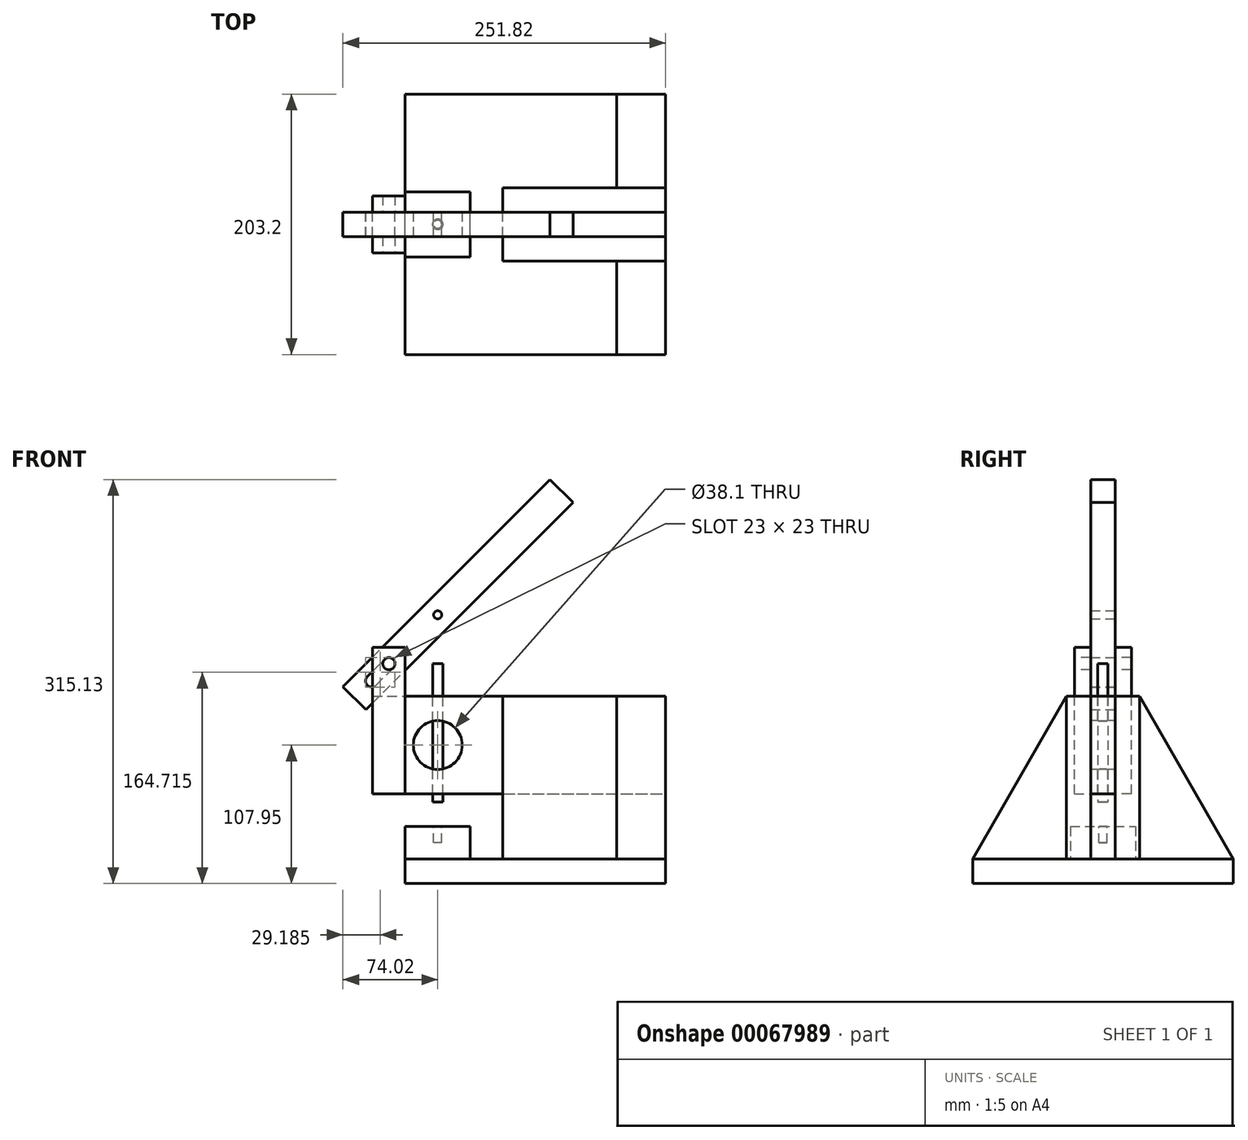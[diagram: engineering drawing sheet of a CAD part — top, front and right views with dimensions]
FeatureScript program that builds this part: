
annotation { "Feature Type Name" : "Feature", "Feature Type Description" : "" }
export const myFeature = defineFeature(function(context is Context, id is Id, definition is map)
    precondition{}
    {
        {
            var Q0;
            Q0=qCreatedBy(makeId("Front.planeOp"),FACE);
            var sketch = newSketch(context, id + "F0", { "sketchPlane" : qUnion([Q0])});
            skLineSegment(sketch, "E0.rect.bottom", {"start": v(101.6, 0) * mm, "end": v(-101.6, 0) * mm});
            skLineSegment(sketch, "E0.rect.top", {"start": v(101.6, 19.05) * mm, "end": v(-101.6, 19.05) * mm});
            skLineSegment(sketch, "E0.rect.left", {"start": v(101.6, 0) * mm, "end": v(101.6, 19.05) * mm});
            skLineSegment(sketch, "E0.rect.right", {"start": v(-101.6, 0) * mm, "end": v(-101.6, 19.05) * mm});
            skPoint(sketch, "E0.rect.middle", {"position": v(0, 9.53) * mm});
            skSolve(sketch);
        }
        {
            var Q0;
            Q0=makeQuery(id+"F0.imprint","IMPRINT",FACE,{"disambiguationData":[TD([[makeQuery(id+"F0.imprint","IMPRINT",EDGE,{"derivedFrom":sQuery(id+"F0.wireOp",EDGE,"E0.rect.bottom")}),-1.0]])]});
            extrude(context, id + "F1", {"entities" : qUnion([Q0]), "endBound" : BoundingType.SYMMETRIC, "depth" : 203.2 * mm});
        }
        {
            var Q0;
            Q0=qCreatedBy(makeId("Front.planeOp"),FACE);
            var sketch = newSketch(context, id + "F2", { "sketchPlane" : qUnion([Q0])});
            skLineSegment(sketch, "E1.bottom", {"start": v(-25.4, 69.85) * mm, "end": v(101.6, 69.85) * mm});
            skLineSegment(sketch, "E1.top", {"start": v(-25.4, 19.05) * mm, "end": v(101.6, 19.05) * mm});
            skLineSegment(sketch, "E1.left", {"start": v(-25.4, 69.85) * mm, "end": v(-25.4, 19.05) * mm});
            skLineSegment(sketch, "E1.right", {"start": v(101.6, 69.85) * mm, "end": v(101.6, 19.05) * mm});
            skLineSegment(sketch, "E2.0", {"start": v(101.6, 19.05) * mm, "end": v(-101.6, 19.05) * mm, "construction": true});
            skSolve(sketch);
        }
        {
            var Q0;
            Q0=makeQuery(id+"F2.imprint","IMPRINT",FACE,{"disambiguationData":[TD([[makeQuery(id+"F2.imprint","IMPRINT",EDGE,{"derivedFrom":sQuery(id+"F2.wireOp",EDGE,"E1.bottom")}),-1.0]])]});
            extrude(context, id + "F3", {"entities" : qUnion([Q0]), "endBound" : BoundingType.SYMMETRIC, "depth" : 19.05 * mm});
        }
        {
            var Q0;
            Q0=qCreatedBy(makeId("Front.planeOp"),FACE);
            var sketch = newSketch(context, id + "F4", { "sketchPlane" : qUnion([Q0])});
            skLineSegment(sketch, "E3.bottom", {"start": v(-127, 146.05) * mm, "end": v(101.6, 146.05) * mm});
            skLineSegment(sketch, "E3.top", {"start": v(-127, 69.85) * mm, "end": v(101.6, 69.85) * mm});
            skLineSegment(sketch, "E3.left", {"start": v(-127, 146.05) * mm, "end": v(-127, 69.85) * mm});
            skLineSegment(sketch, "E3.right", {"start": v(101.6, 146.05) * mm, "end": v(101.6, 69.85) * mm});
            skLineSegment(sketch, "E4.0", {"start": v(-25.4, 69.85) * mm, "end": v(101.6, 69.85) * mm, "construction": true});
            skSolve(sketch);
        }
        {
            var Q0;
            Q0=makeQuery(id+"F4.imprint","IMPRINT",FACE,{"disambiguationData":[TD([[makeQuery(id+"F4.imprint","IMPRINT",EDGE,{"derivedFrom":sQuery(id+"F4.wireOp",EDGE,"E3.bottom")}),-1.0]])]});
            extrude(context, id + "F5", {"entities" : qUnion([Q0]), "endBound" : BoundingType.SYMMETRIC, "depth" : 19.05 * mm});
        }
        {
            var Q0;
            Q0=makeQuery(id+"F5.opExtrude","CAP_FACE",FACE,{"disambiguationData":[OSD([sQuery(id+"F4.wireOp",EDGE,"E3.bottom"),sQuery(id+"F4.wireOp",EDGE,"E3.top"),sQuery(id+"F4.wireOp",EDGE,"E3.left"),sQuery(id+"F4.wireOp",EDGE,"E3.right")])],"isStart":false});
            var sketch = newSketch(context, id + "F6", { "sketchPlane" : qUnion([Q0])});
            skLineSegment(sketch, "E5.0", {"start": v(-25.4, 69.85) * mm, "end": v(-25.4, 19.05) * mm, "construction": true});
            skLineSegment(sketch, "E6.bottom", {"start": v(101.6, 146.05) * mm, "end": v(-25.4, 146.05) * mm});
            skLineSegment(sketch, "E6.top", {"start": v(101.6, 19.05) * mm, "end": v(-25.4, 19.05) * mm});
            skLineSegment(sketch, "E6.left", {"start": v(101.6, 146.05) * mm, "end": v(101.6, 19.05) * mm});
            skLineSegment(sketch, "E6.right", {"start": v(-25.4, 146.05) * mm, "end": v(-25.4, 19.05) * mm});
            skSolve(sketch);
        }
        {
            var Q0;
            Q0 = qSketchRegion(id + "F6", true);
            extrude(context, id + "F7", {"entities" : qUnion([Q0]), "depth" : 19.05 * mm});
        }
        {
            var Q0;
            Q0=makeQuery(id+"F7.opExtrude","SWEPT_BODY",BODY,{"disambiguationData":[OSD([sQuery(id+"F6.wireOp",EDGE,"E6.bottom"),sQuery(id+"F6.wireOp",EDGE,"E6.top"),sQuery(id+"F6.wireOp",EDGE,"E6.left"),sQuery(id+"F6.wireOp",EDGE,"E6.right")])]});
            var Q1;
            Q1=qCreatedBy(makeId("Front.planeOp"),FACE);
            mirror(context, id + "F8", {"entities" : qUnion([Q0]), "mirrorPlane" : qUnion([Q1])});
        }
        {
            var Q0;
            Q0=makeQuery(id+"F7.opExtrude","SWEPT_FACE",FACE,{"disambiguationData":[OSD([sQuery(id+"F6.wireOp",EDGE,"E6.left")])]});
            var sketch = newSketch(context, id + "F9", { "sketchPlane" : qUnion([Q0])});
            skLineSegment(sketch, "E7.0", {"start": v(-101.6, 0) * mm, "end": v(-101.6, 19.05) * mm, "construction": true});
            skLineSegment(sketch, "E8.0", {"start": v(-28.58, 146.05) * mm, "end": v(-28.58, 19.05) * mm});
            skLineSegment(sketch, "E9", {"start": v(-28.58, 146.05) * mm, "end": v(-101.6, 19.05) * mm});
            skLineSegment(sketch, "E10", {"start": v(-28.58, 19.05) * mm, "end": v(-101.6, 19.05) * mm});
            skSolve(sketch);
        }
        {
            var Q0;
            Q0 = qSketchRegion(id + "F9", true);
            extrude(context, id + "F10", {"entities" : qUnion([Q0]), "oppositeDirection" : true, "depth" : 38.1 * mm});
        }
        {
            var Q0;
            Q0=makeQuery(id+"F10.opExtrude","SWEPT_BODY",BODY,{"disambiguationData":[OSD([sQuery(id+"F9.wireOp",EDGE,"E8.0"),sQuery(id+"F9.wireOp",EDGE,"E9"),sQuery(id+"F9.wireOp",EDGE,"E10")])]});
            var Q1;
            Q1=qCreatedBy(makeId("Front.planeOp"),FACE);
            mirror(context, id + "F11", {"entities" : qUnion([Q0]), "mirrorPlane" : qUnion([Q1])});
        }
        {
            var Q0;
            Q0=makeQuery(id+"F1.opExtrude","SWEPT_FACE",FACE,{"disambiguationData":[OSD([sQuery(id+"F0.wireOp",EDGE,"E0.rect.top")])]});
            var sketch = newSketch(context, id + "F12", { "sketchPlane" : qUnion([Q0])});
            skLineSegment(sketch, "E11.rect.bottom", {"start": v(-101.6, -25.4) * mm, "end": v(-50.8, -25.4) * mm});
            skLineSegment(sketch, "E11.rect.top", {"start": v(-101.6, 25.4) * mm, "end": v(-50.8, 25.4) * mm});
            skLineSegment(sketch, "E11.rect.left", {"start": v(-101.6, -25.4) * mm, "end": v(-101.6, 25.4) * mm});
            skLineSegment(sketch, "E11.rect.right", {"start": v(-50.8, -25.4) * mm, "end": v(-50.8, 25.4) * mm});
            skPoint(sketch, "E11.rect.middle", {"position": v(-76.2, 0) * mm});
            skSolve(sketch);
        }
        {
            var Q0;
            Q0 = qSketchRegion(id + "F12", true);
            extrude(context, id + "F13", {"entities" : qUnion([Q0]), "depth" : 25.4 * mm});
        }
        {
            var Q0;
            Q0=makeQuery(id+"F13.opExtrude","CAP_FACE",FACE,{"disambiguationData":[OSD([sQuery(id+"F12.wireOp",EDGE,"E11.rect.bottom"),sQuery(id+"F12.wireOp",EDGE,"E11.rect.top"),sQuery(id+"F12.wireOp",EDGE,"E11.rect.left"),sQuery(id+"F12.wireOp",EDGE,"E11.rect.right")])],"isStart":false});
            var sketch = newSketch(context, id + "F14", { "sketchPlane" : qUnion([Q0])});
            skLineSegment(sketch, "E12", {"start": v(-101.6, 25.4) * mm, "end": v(-50.8, -25.4) * mm, "construction": true});
            skCircle(sketch, "E13", {"center": v(-76.2, 0) * mm, "radius": 3.18 * mm});
            skSolve(sketch);
        }
        {
            var Q0;
            Q0 = qSketchRegion(id + "F14", true);
            extrude(context, id + "F15", {"entities" : qUnion([Q0]), "operationType" : NewBodyOperationType.REMOVE, "oppositeDirection" : true, "depth" : 12.7 * mm});
        }
        {
            var Q0;
            Q0=makeQuery(id+"F5.opExtrude","SWEPT_FACE",FACE,{"disambiguationData":[OSD([sQuery(id+"F4.wireOp",EDGE,"E3.bottom")])]});
            var sketch = newSketch(context, id + "F16", { "sketchPlane" : qUnion([Q0])});
            skCircle(sketch, "E14.0", {"center": v(-76.2, 0) * mm, "radius": 3.18 * mm, "construction": true});
            skCircle(sketch, "E15", {"center": v(-76.2, 0) * mm, "radius": 4 * mm});
            skSolve(sketch);
        }
        {
            var Q0;
            Q0=makeQuery(id+"F16.imprint","IMPRINT",FACE,{"disambiguationData":[TD([[makeQuery(id+"F16.imprint","IMPRINT",EDGE,{"derivedFrom":sQuery(id+"F16.wireOp",EDGE,"E15")}),1.0]])]});
            extrude(context, id + "F17", {"entities" : qUnion([Q0]), "operationType" : NewBodyOperationType.REMOVE, "endBound" : BoundingType.UP_TO_NEXT, "oppositeDirection" : true, "depth" : 25.4 * mm});
        }
        {
            var Q0;
            Q0=makeQuery(id+"F5.opExtrude","CAP_FACE",FACE,{"disambiguationData":[OSD([sQuery(id+"F4.wireOp",EDGE,"E3.bottom"),sQuery(id+"F4.wireOp",EDGE,"E3.top"),sQuery(id+"F4.wireOp",EDGE,"E3.left"),sQuery(id+"F4.wireOp",EDGE,"E3.right")])],"isStart":false});
            var sketch = newSketch(context, id + "F18", { "sketchPlane" : qUnion([Q0])});
            skLineSegment(sketch, "E16.0", {"start": v(-80.2, 146.05) * mm, "end": v(-72.2, 146.05) * mm, "construction": true});
            skLineSegment(sketch, "E17", {"start": v(-76.2, 146.05) * mm, "end": v(-76.2, 69.85) * mm, "construction": true});
            skCircle(sketch, "E18", {"center": v(-76.2, 107.95) * mm, "radius": 19.05 * mm});
            skSolve(sketch);
        }
        {
            var Q0;
            Q0=makeQuery(id+"F18.imprint","IMPRINT",FACE,{"disambiguationData":[TD([[makeQuery(id+"F18.imprint","IMPRINT",EDGE,{"derivedFrom":sQuery(id+"F18.wireOp",EDGE,"E18")}),1.0]])]});
            var Q1;
            Q1=sQuery(id+"F18.wireOp",EDGE,"E18");
            extrude(context, id + "F19", {"entities" : qUnion([Q0]), "operationType" : NewBodyOperationType.REMOVE, "surfaceEntities" : qUnion([Q1]), "endBound" : BoundingType.THROUGH_ALL, "oppositeDirection" : true, "depth" : 25.4 * mm});
        }
        {
            var Q0;
            Q0=makeQuery(id+"F5.opExtrude","CAP_FACE",FACE,{"disambiguationData":[OSD([sQuery(id+"F4.wireOp",EDGE,"E3.bottom"),sQuery(id+"F4.wireOp",EDGE,"E3.top"),sQuery(id+"F4.wireOp",EDGE,"E3.left"),sQuery(id+"F4.wireOp",EDGE,"E3.right")])],"isStart":false});
            var sketch = newSketch(context, id + "F20", { "sketchPlane" : qUnion([Q0])});
            skLineSegment(sketch, "E19.bottom", {"start": v(-127, 69.85) * mm, "end": v(-101.6, 69.85) * mm});
            skLineSegment(sketch, "E19.top", {"start": v(-127, 184.15) * mm, "end": v(-101.6, 184.15) * mm});
            skLineSegment(sketch, "E19.left", {"start": v(-127, 69.85) * mm, "end": v(-127, 184.15) * mm});
            skLineSegment(sketch, "E19.right", {"start": v(-101.6, 69.85) * mm, "end": v(-101.6, 184.15) * mm});
            skSolve(sketch);
        }
        {
            var Q0;
            {var subQ0=sQuery(id+"F20.wireOp",EDGE,"E19.top");Q0=makeQuery(id+"F20.imprint","IMPRINT",FACE,{"disambiguationData":[TD([[makeQuery(id+"F20.imprint","IMPRINT",EDGE,{"derivedFrom":subQ0}),-1.0]])]});}
            var Q1;
            {var subQ7=sQuery(id+"F20.wireOp",EDGE,"E19.bottom");Q1=makeQuery(id+"F20.imprint","IMPRINT",FACE,{"disambiguationData":[TD([[makeQuery(id+"F20.imprint","IMPRINT",EDGE,{"derivedFrom":subQ7}),1.0]])]});}
            var Q2;
            {var subQ0=sQuery(id+"F20.wireOp",EDGE,"E19.right");var subQ1=makeQuery(id+"F19.boolean.opBoolean","COPY",EDGE,{"derivedFrom":makeQuery(id+"F19.opExtrude","CAP_EDGE",EDGE,{"disambiguationData":[OSD([sQuery(id+"F18.wireOp",EDGE,"E18")])],"isStart":true})});var subQ2=makeQuery(id+"F20.imprint","INTERSECT",VERTEX,{"disambiguationData":[OD(0.0)],"derivedFrom":[subQ1,subQ0]});Q2=makeQuery(id+"F20.imprint","IMPRINT",FACE,{"disambiguationData":[TD([[makeQuery(id+"F20.imprint","IMPRINT",EDGE,{"disambiguationData":[TD([[subQ2,-1.0]])],"derivedFrom":subQ0}),1.0]])]});}
            extrude(context, id + "F21", {"entities" : qUnion([Q0, Q1, Q2]), "depth" : 12.7 * mm});
        }
        {
            var Q0;
            Q0=makeQuery(id+"F21.opExtrude","SWEPT_BODY",BODY,{"disambiguationData":[OSD([sQuery(id+"F20.wireOp",EDGE,"E19.bottom"),sQuery(id+"F20.wireOp",EDGE,"E19.top"),sQuery(id+"F20.wireOp",EDGE,"E19.left"),sQuery(id+"F20.wireOp",EDGE,"E19.right")])]});
            var Q1;
            Q1=qCreatedBy(makeId("Front.planeOp"),FACE);
            mirror(context, id + "F22", {"entities" : qUnion([Q0]), "mirrorPlane" : qUnion([Q1])});
        }
        {
            var Q0;
            Q0=makeQuery(id+"F21.opExtrude","CAP_FACE",FACE,{"disambiguationData":[OSD([sQuery(id+"F20.wireOp",EDGE,"E19.bottom"),sQuery(id+"F20.wireOp",EDGE,"E19.top"),sQuery(id+"F20.wireOp",EDGE,"E19.left"),sQuery(id+"F20.wireOp",EDGE,"E19.right")])],"isStart":false});
            var sketch = newSketch(context, id + "F23", { "sketchPlane" : qUnion([Q0])});
            skLineSegment(sketch, "E20.0", {"start": v(-127, 184.15) * mm, "end": v(-101.6, 184.15) * mm, "construction": true});
            skCircle(sketch, "E21", {"center": v(-114.3, 171.45) * mm, "radius": 4.76 * mm});
            skPoint(sketch, "E21.centerSnap0", {"position": v(-114.3, 184.15) * mm});
            skSolve(sketch);
        }
        {
            var Q0;
            Q0=makeQuery(id+"F23.imprint","IMPRINT",FACE,{"disambiguationData":[TD([[makeQuery(id+"F23.imprint","IMPRINT",EDGE,{"derivedFrom":sQuery(id+"F23.wireOp",EDGE,"E21")}),1.0]])]});
            extrude(context, id + "F24", {"entities" : qUnion([Q0]), "operationType" : NewBodyOperationType.REMOVE, "endBound" : BoundingType.THROUGH_ALL, "oppositeDirection" : true, "depth" : 25.4 * mm});
        }
        {
            var Q0;
            Q0=qCreatedBy(makeId("Front.planeOp"),FACE);
            var sketch = newSketch(context, id + "F25", { "sketchPlane" : qUnion([Q0])});
            skArc(sketch, "E22.0", {"start": v(-110.93, 168.08) * mm, "mid": v(-110.93, 174.82) * mm, "end": v(-117.67, 174.82) * mm});
            skLineSegment(sketch, "E23", {"start": v(-114.3, 171.45) * mm, "end": v(29.38, 315.13) * mm, "construction": true});
            skLineSegment(sketch, "E24.0", {"start": v(-132.26, 135.53) * mm, "end": v(29.38, 297.17) * mm});
            skLineSegment(sketch, "E25.0", {"start": v(-150.22, 153.49) * mm, "end": v(11.42, 315.13) * mm});
            skLineSegment(sketch, "E26", {"start": v(-150.22, 153.49) * mm, "end": v(-132.26, 135.53) * mm});
            skLineSegment(sketch, "E27", {"start": v(11.42, 315.13) * mm, "end": v(29.38, 297.17) * mm});
            skLineSegment(sketch, "E28", {"start": v(-114.3, 171.45) * mm, "end": v(-127.77, 157.98) * mm, "construction": true});
            skArc(sketch, "E29", {"start": v(-131.14, 161.35) * mm, "mid": v(-131.14, 154.61) * mm, "end": v(-124.4, 154.61) * mm});
            skLineSegment(sketch, "E30", {"start": v(-131.14, 161.35) * mm, "end": v(-117.67, 174.82) * mm});
            skLineSegment(sketch, "E31", {"start": v(-124.4, 154.61) * mm, "end": v(-110.93, 168.08) * mm});
            skLineSegment(sketch, "E32.0", {"start": v(-80.2, 146.05) * mm, "end": v(-72.2, 146.05) * mm, "construction": true});
            skLineSegment(sketch, "E33", {"start": v(-76.2, 146.05) * mm, "end": v(-76.2, 209.55) * mm, "construction": true});
            skCircle(sketch, "E34", {"center": v(-76.2, 209.55) * mm, "radius": 3.18 * mm});
            skSolve(sketch);
        }
        {
            var Q0;
            Q0=makeQuery(id+"F25.imprint","IMPRINT",FACE,{"disambiguationData":[TD([[makeQuery(id+"F25.imprint","IMPRINT",EDGE,{"derivedFrom":sQuery(id+"F25.wireOp",EDGE,"E22.0")}),-1.0]])]});
            extrude(context, id + "F26", {"entities" : qUnion([Q0]), "endBound" : BoundingType.SYMMETRIC, "depth" : 19.05 * mm});
        }
        {
            var Q0;
            Q0=makeQuery(id+"F5.opExtrude","SWEPT_FACE",FACE,{"disambiguationData":[OSD([sQuery(id+"F4.wireOp",EDGE,"E3.bottom")])]});
            var sketch = newSketch(context, id + "F27", { "sketchPlane" : qUnion([Q0])});
            skCircle(sketch, "E35.0", {"center": v(-76.2, 0) * mm, "radius": 4 * mm});
            skSolve(sketch);
        }
        {
            var Q0;
            Q0=makeQuery(id+"F27.imprint","IMPRINT",FACE,{"disambiguationData":[TD([[makeQuery(id+"F27.imprint","IMPRINT",EDGE,{"derivedFrom":sQuery(id+"F27.wireOp",EDGE,"E35.0")}),1.0]])]});
            extrude(context, id + "F28", {"entities" : qUnion([Q0]), "depth" : 25.4 * mm, "hasSecondDirection" : true, "secondDirectionOppositeDirection" : true, "secondDirectionDepth" : 82.55 * mm});
        }
    });
